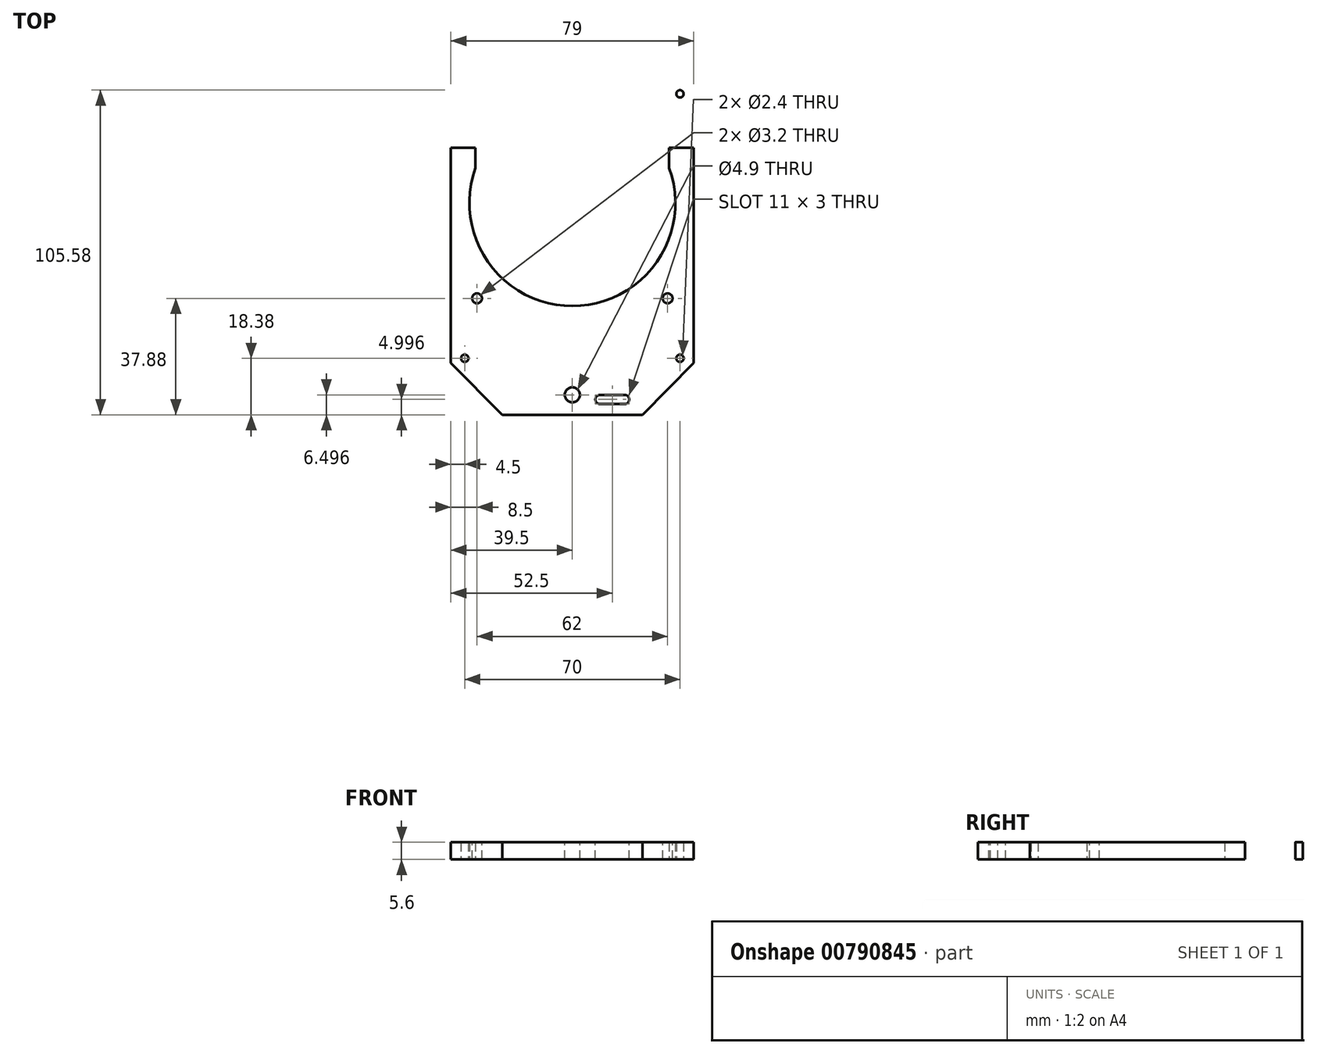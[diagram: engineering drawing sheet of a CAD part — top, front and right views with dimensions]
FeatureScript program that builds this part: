
annotation { "Feature Type Name" : "Feature", "Feature Type Description" : "" }
export const myFeature = defineFeature(function(context is Context, id is Id, definition is map)
    precondition{}
    {
        {
            var Q0;
            Q0=qCreatedBy(makeId("Top.planeOp"),FACE);
            var sketch = newSketch(context, id + "F0", { "sketchPlane" : qUnion([Q0])});
            skLineSegment(sketch, "E0.bottom", {"start": v(36.5, -47.5) * mm, "end": v(-36.5, -47.5) * mm, "construction": true});
            skLineSegment(sketch, "E0.top", {"start": v(36.5, 47.5) * mm, "end": v(-36.5, 47.5) * mm, "construction": true});
            skLineSegment(sketch, "E0.left", {"start": v(39.5, -44.5) * mm, "end": v(39.5, 44.5) * mm});
            skLineSegment(sketch, "E0.right", {"start": v(-39.5, -44.5) * mm, "end": v(-39.5, 44.5) * mm});
            skPoint(sketch, "E0.middle", {"position": v(0, 0) * mm});
            skCircle(sketch, "E1", {"center": v(35, -43) * mm, "radius": 1.2 * mm});
            skLineSegment(sketch, "E2", {"start": v(0, 0) * mm, "end": v(59.48, 0) * mm, "construction": true});
            skLineSegment(sketch, "E3", {"start": v(0, -16.17) * mm, "end": v(0, 69.78) * mm, "construction": true});
            skCircle(sketch, "E4.MirrorC", {"center": v(35, 43) * mm, "radius": 1.2 * mm});
            skCircle(sketch, "E5.MirrorC", {"center": v(-35, 43) * mm, "radius": 1.2 * mm});
            skCircle(sketch, "E6.MirrorC", {"center": v(-35, -43) * mm, "radius": 1.2 * mm});
            skPoint(sketch, "E7.visualSharp", {"position": v(-39.5, 47.5) * mm});
            skArc(sketch, "E7.filletArc", {"start": v(-36.5, 47.5) * mm, "mid": v(-38.62, 46.62) * mm, "end": v(-39.5, 44.5) * mm, "construction": true});
            skPoint(sketch, "E8.visualSharp", {"position": v(39.5, 47.5) * mm});
            skArc(sketch, "E8.filletArc", {"start": v(39.5, 44.5) * mm, "mid": v(38.62, 46.62) * mm, "end": v(36.5, 47.5) * mm, "construction": true});
            skPoint(sketch, "E9.visualSharp", {"position": v(39.5, -47.5) * mm});
            skArc(sketch, "E9.filletArc", {"start": v(36.5, -47.5) * mm, "mid": v(38.62, -46.62) * mm, "end": v(39.5, -44.5) * mm, "construction": true});
            skPoint(sketch, "E10.visualSharp", {"position": v(-39.5, -47.5) * mm});
            skArc(sketch, "E10.filletArc", {"start": v(-39.5, -44.5) * mm, "mid": v(-38.62, -46.62) * mm, "end": v(-36.5, -47.5) * mm, "construction": true});
            skCircle(sketch, "E11", {"center": v(0, 7.5) * mm, "radius": 33.5 * mm});
            skLineSegment(sketch, "E12.bottom", {"start": v(31, -23.5) * mm, "end": v(-31, -23.5) * mm, "construction": true});
            skLineSegment(sketch, "E12.top", {"start": v(31, 38.5) * mm, "end": v(-31, 38.5) * mm, "construction": true});
            skLineSegment(sketch, "E12.left", {"start": v(31, -23.5) * mm, "end": v(31, 38.5) * mm, "construction": true});
            skLineSegment(sketch, "E12.right", {"start": v(-31, -23.5) * mm, "end": v(-31, 38.5) * mm, "construction": true});
            skLineSegment(sketch, "E13", {"start": v(0, 61.38) * mm, "end": v(22.8, 61.38) * mm});
            skLineSegment(sketch, "E14", {"start": v(22.8, 61.38) * mm, "end": v(39.5, 44.5) * mm});
            skLineSegment(sketch, "E15.MirrorCS", {"start": v(-22.8, 61.38) * mm, "end": v(-39.5, 44.5) * mm});
            skLineSegment(sketch, "E16.MirrorCS", {"start": v(0, 61.38) * mm, "end": v(-22.8, 61.38) * mm});
            skCircle(sketch, "E17", {"center": v(0, 54.88) * mm, "radius": 2.05 * mm});
            skLineSegment(sketch, "E18.MirrorCS", {"start": v(-22.8, -61.38) * mm, "end": v(-39.5, -44.5) * mm});
            skLineSegment(sketch, "E19.MirrorCS", {"start": v(0, -61.38) * mm, "end": v(-22.8, -61.38) * mm});
            skLineSegment(sketch, "E20.MirrorCS", {"start": v(0, -61.38) * mm, "end": v(22.8, -61.38) * mm});
            skLineSegment(sketch, "E21.MirrorCS", {"start": v(22.8, -61.38) * mm, "end": v(39.5, -44.5) * mm});
            skArc(sketch, "E22.MirrorCS", {"start": v(-39.5, 44.5) * mm, "mid": v(-38.62, 46.62) * mm, "end": v(-36.5, 47.5) * mm, "construction": true});
            skArc(sketch, "E23.MirrorCS", {"start": v(36.5, 47.5) * mm, "mid": v(38.62, 46.62) * mm, "end": v(39.5, 44.5) * mm, "construction": true});
            skCircle(sketch, "E24.MirrorC", {"center": v(0, -54.88) * mm, "radius": 2.05 * mm});
            skLineSegment(sketch, "E25", {"start": v(-51.45, 25.5) * mm, "end": v(82.98, 25.5) * mm, "construction": true});
            skLineSegment(sketch, "E26", {"start": v(-59.5, -9.5) * mm, "end": v(81.33, -9.5) * mm, "construction": true});
            skLineSegment(sketch, "E27", {"start": v(31.5, 25.5) * mm, "end": v(31.5, -9.5) * mm});
            skLineSegment(sketch, "E28.MirrorCS", {"start": v(-31.5, 25.5) * mm, "end": v(-31.5, -9.5) * mm});
            skLineSegment(sketch, "E29", {"start": v(31.5, 25.5) * mm, "end": v(39.5, 25.5) * mm});
            skLineSegment(sketch, "E30", {"start": v(31.5, -9.5) * mm, "end": v(39.5, -9.5) * mm});
            skLineSegment(sketch, "E31", {"start": v(-31.5, -9.5) * mm, "end": v(-39.5, -9.5) * mm});
            skLineSegment(sketch, "E32", {"start": v(-31.5, 25.5) * mm, "end": v(-39.5, 25.5) * mm});
            skSolve(sketch);
        }
        {
            var Q0;
            Q0=makeQuery(id+"F0.imprint","IMPRINT",FACE,{"disambiguationData":[TD([[makeQuery(id+"F0.imprint","IMPRINT",EDGE,{"derivedFrom":sQuery(id+"F0.wireOp",EDGE,"E4.MirrorC")}),1.0]])]});
            var Q1;
            Q1=makeQuery(id+"F0.imprint","IMPRINT",FACE,{"disambiguationData":[TD([[makeQuery(id+"F0.imprint","IMPRINT",EDGE,{"derivedFrom":sQuery(id+"F0.wireOp",EDGE,"E1")}),-1.0]])]});
            var Q2;
            {var subQ5=sQuery(id+"F0.wireOp",EDGE,"E31");Q2=makeQuery(id+"F0.imprint","IMPRINT",FACE,{"disambiguationData":[TD([[makeQuery(id+"F0.imprint","IMPRINT",EDGE,{"derivedFrom":subQ5}),-1.0]])]});}
            var Q3;
            {var subQ0=sQuery(id+"F0.wireOp",EDGE,"E29");Q3=makeQuery(id+"F0.imprint","IMPRINT",FACE,{"disambiguationData":[TD([[makeQuery(id+"F0.imprint","IMPRINT",EDGE,{"derivedFrom":subQ0}),-1.0]])]});}
            extrude(context, id + "F1", {"entities" : qUnion([Q0, Q1, Q2, Q3]), "depth" : 5.6 * mm, "offsetDistance" : 25 * mm});
        }
        {
            var Q0;
            Q0=makeQuery(id+"F1.opExtrude","CAP_FACE",FACE,{"disambiguationData":[OSD([sQuery(id+"F0.wireOp",EDGE,"E0.left"),sQuery(id+"F0.wireOp",EDGE,"E0.right"),sQuery(id+"F0.wireOp",EDGE,"E1"),sQuery(id+"F0.wireOp",EDGE,"E4.MirrorC"),sQuery(id+"F0.wireOp",EDGE,"E5.MirrorC"),sQuery(id+"F0.wireOp",EDGE,"E6.MirrorC"),sQuery(id+"F0.wireOp",EDGE,"E11"),sQuery(id+"F0.wireOp",EDGE,"E13"),sQuery(id+"F0.wireOp",EDGE,"E14"),sQuery(id+"F0.wireOp",EDGE,"E15.MirrorCS"),sQuery(id+"F0.wireOp",EDGE,"E16.MirrorCS"),sQuery(id+"F0.wireOp",EDGE,"E17"),sQuery(id+"F0.wireOp",EDGE,"E18.MirrorCS"),sQuery(id+"F0.wireOp",EDGE,"E19.MirrorCS"),sQuery(id+"F0.wireOp",EDGE,"E20.MirrorCS"),sQuery(id+"F0.wireOp",EDGE,"E21.MirrorCS"),sQuery(id+"F0.wireOp",EDGE,"E24.MirrorC")])],"isStart":false});
            var sketch = newSketch(context, id + "F2", { "sketchPlane" : qUnion([Q0])});
            skCircle(sketch, "E33", {"center": v(-31, 38.5) * mm, "radius": 1.6 * mm});
            skCircle(sketch, "E34", {"center": v(31, 38.5) * mm, "radius": 1.6 * mm});
            skCircle(sketch, "E35", {"center": v(-31, -23.5) * mm, "radius": 1.6 * mm});
            skCircle(sketch, "E36", {"center": v(31, -23.5) * mm, "radius": 1.6 * mm});
            skCircle(sketch, "E37", {"center": v(0, 54.88) * mm, "radius": 2.45 * mm});
            skCircle(sketch, "E38.MirrorC", {"center": v(0, -54.88) * mm, "radius": 2.45 * mm});
            skLineSegment(sketch, "E39.bottom", {"start": v(9, 57.88) * mm, "end": v(17, 57.88) * mm});
            skLineSegment(sketch, "E39.top", {"start": v(9, 54.88) * mm, "end": v(17, 54.88) * mm});
            skLineSegment(sketch, "E39.left", {"start": v(9, 57.88) * mm, "end": v(9, 54.88) * mm});
            skLineSegment(sketch, "E39.right", {"start": v(17, 57.88) * mm, "end": v(17, 54.88) * mm});
            skCircle(sketch, "E40", {"center": v(17, 56.38) * mm, "radius": 1.5 * mm});
            skCircle(sketch, "E41", {"center": v(9, 56.38) * mm, "radius": 1.5 * mm});
            skCircle(sketch, "E42.MirrorC", {"center": v(9, -56.38) * mm, "radius": 1.5 * mm});
            skLineSegment(sketch, "E43.MirrorCS", {"start": v(9, -57.88) * mm, "end": v(17, -57.88) * mm});
            skLineSegment(sketch, "E44.MirrorCS", {"start": v(9, -54.88) * mm, "end": v(17, -54.88) * mm});
            skCircle(sketch, "E45.MirrorC", {"center": v(17, -56.38) * mm, "radius": 1.5 * mm});
            skSolve(sketch);
        }
        {
            var Q0;
            Q0 = qSketchRegion(id + "F2", true);
            extrude(context, id + "F3", {"entities" : qUnion([Q0]), "operationType" : NewBodyOperationType.REMOVE, "oppositeDirection" : true, "depth" : 25 * mm, "offsetDistance" : 25 * mm});
        }
    });
